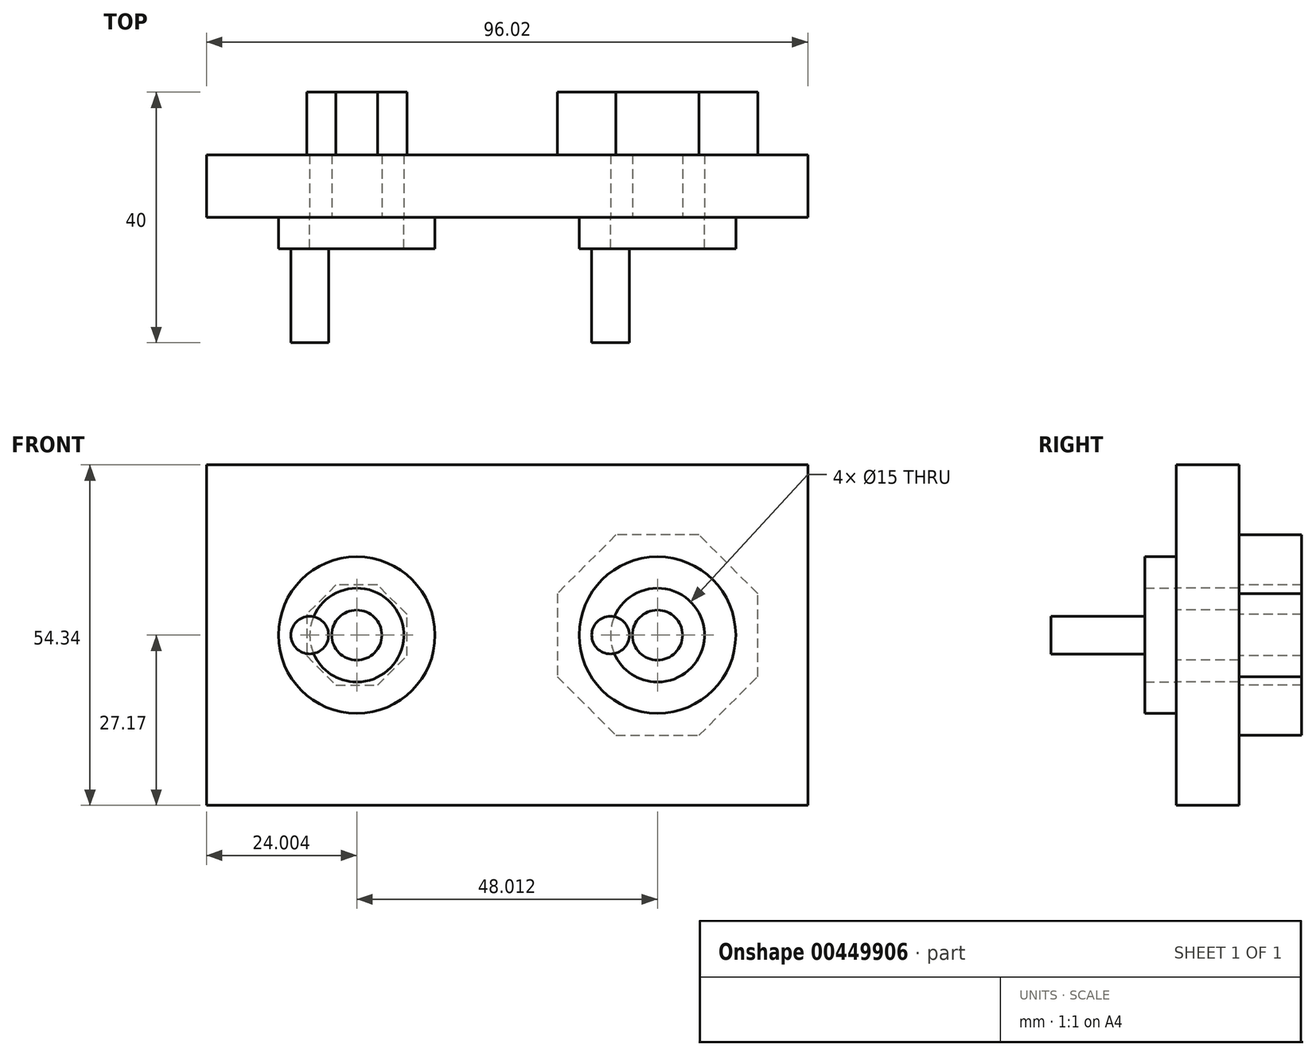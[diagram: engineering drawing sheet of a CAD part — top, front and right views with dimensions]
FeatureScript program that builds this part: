
annotation { "Feature Type Name" : "Feature", "Feature Type Description" : "" }
export const myFeature = defineFeature(function(context is Context, id is Id, definition is map)
    precondition{}
    {
        {
            var Q0;
            Q0=qCreatedBy(makeId("Front.planeOp"),FACE);
            var sketch = newSketch(context, id + "F0", { "sketchPlane" : qUnion([Q0])});
            skLineSegment(sketch, "E0.bottom", {"start": v(-48.01, 27.17) * mm, "end": v(48.01, 27.17) * mm});
            skLineSegment(sketch, "E0.top", {"start": v(-48.01, -27.17) * mm, "end": v(48.01, -27.17) * mm});
            skLineSegment(sketch, "E0.left", {"start": v(-48.01, 27.17) * mm, "end": v(-48.01, -27.17) * mm});
            skLineSegment(sketch, "E0.right", {"start": v(48.01, 27.17) * mm, "end": v(48.01, -27.17) * mm});
            skPoint(sketch, "E0.middle", {"position": v(0, 0) * mm});
            skSolve(sketch);
        }
        {
            var Q0;
            Q0=makeQuery(id+"F0.imprint","IMPRINT",FACE,{"disambiguationData":[TD([[makeQuery(id+"F0.imprint","IMPRINT",EDGE,{"derivedFrom":sQuery(id+"F0.wireOp",EDGE,"E0.bottom")}),-1.0]])]});
            extrude(context, id + "F1", {"entities" : qUnion([Q0]), "depth" : 10 * mm});
        }
        {
            var Q0;
            Q0=makeQuery(id+"F1.opExtrude","CAP_FACE",FACE,{"disambiguationData":[OSD([sQuery(id+"F0.wireOp",EDGE,"E0.bottom"),sQuery(id+"F0.wireOp",EDGE,"E0.top"),sQuery(id+"F0.wireOp",EDGE,"E0.left"),sQuery(id+"F0.wireOp",EDGE,"E0.right")])],"isStart":false});
            var sketch = newSketch(context, id + "F2", { "sketchPlane" : qUnion([Q0])});
            skLineSegment(sketch, "E1", {"start": v(0, 0) * mm, "end": v(-48.01, 0) * mm, "construction": true});
            skLineSegment(sketch, "E2", {"start": v(0, 0) * mm, "end": v(48.01, 0) * mm, "construction": true});
            skCircle(sketch, "E3", {"center": v(-24, 0) * mm, "radius": 7.5 * mm});
            skCircle(sketch, "E4", {"center": v(24, 0) * mm, "radius": 7.5 * mm});
            skSolve(sketch);
        }
        {
            var Q0;
            Q0=makeQuery(id+"F2.imprint","IMPRINT",FACE,{"disambiguationData":[TD([[makeQuery(id+"F2.imprint","IMPRINT",EDGE,{"derivedFrom":sQuery(id+"F2.wireOp",EDGE,"E3")}),1.0]])]});
            var Q1;
            Q1=makeQuery(id+"F2.imprint","IMPRINT",FACE,{"disambiguationData":[TD([[makeQuery(id+"F2.imprint","IMPRINT",EDGE,{"derivedFrom":sQuery(id+"F2.wireOp",EDGE,"E4")}),1.0]])]});
            var Q2;
            Q2=makeQuery(id+"F1.opExtrude","CAP_FACE",FACE,{"disambiguationData":[OSD([sQuery(id+"F0.wireOp",EDGE,"E0.bottom"),sQuery(id+"F0.wireOp",EDGE,"E0.top"),sQuery(id+"F0.wireOp",EDGE,"E0.left"),sQuery(id+"F0.wireOp",EDGE,"E0.right")])],"isStart":true});
            extrude(context, id + "F3", {"entities" : qUnion([Q0, Q1]), "operationType" : NewBodyOperationType.REMOVE, "endBound" : BoundingType.UP_TO_SURFACE, "oppositeDirection" : true, "endBoundEntityFace" : qUnion([Q2]), "depth" : 25 * mm});
        }
        {
            var Q0;
            Q0=makeQuery(id+"F1.opExtrude","CAP_FACE",FACE,{"disambiguationData":[OSD([sQuery(id+"F0.wireOp",EDGE,"E0.bottom"),sQuery(id+"F0.wireOp",EDGE,"E0.top"),sQuery(id+"F0.wireOp",EDGE,"E0.left"),sQuery(id+"F0.wireOp",EDGE,"E0.right")])],"isStart":false});
            var sketch = newSketch(context, id + "F4", { "sketchPlane" : qUnion([Q0])});
            skCircle(sketch, "E5", {"center": v(-24, 0) * mm, "radius": 12.5 * mm});
            skCircle(sketch, "E6", {"center": v(24, 0) * mm, "radius": 12.5 * mm});
            skSolve(sketch);
        }
        {
            var Q0;
            Q0=makeQuery(id+"F4.imprint","IMPRINT",FACE,{"disambiguationData":[TD([[makeQuery(id+"F4.imprint","IMPRINT",EDGE,{"derivedFrom":sQuery(id+"F4.wireOp",EDGE,"E5")}),1.0]])]});
            var Q1;
            Q1=makeQuery(id+"F4.imprint","IMPRINT",FACE,{"disambiguationData":[TD([[makeQuery(id+"F4.imprint","IMPRINT",EDGE,{"derivedFrom":sQuery(id+"F4.wireOp",EDGE,"E6")}),1.0]])]});
            var Q2;
            Q2=makeQuery(id+"F4.imprint","IMPRINT",FACE,{"disambiguationData":[TD([[makeQuery(id+"F4.imprint","IMPRINT",EDGE,{"derivedFrom":makeQuery(id+"F3.boolean.opBoolean","COPY",EDGE,{"derivedFrom":makeQuery(id+"F3.opExtrude","CAP_EDGE",EDGE,{"disambiguationData":[OSD([sQuery(id+"F2.wireOp",EDGE,"E4")])],"isStart":true})})}),1.0]])]});
            var Q3;
            Q3=makeQuery(id+"F4.imprint","IMPRINT",FACE,{"disambiguationData":[TD([[makeQuery(id+"F4.imprint","IMPRINT",EDGE,{"derivedFrom":makeQuery(id+"F3.boolean.opBoolean","COPY",EDGE,{"derivedFrom":makeQuery(id+"F3.opExtrude","CAP_EDGE",EDGE,{"disambiguationData":[OSD([sQuery(id+"F2.wireOp",EDGE,"E3")])],"isStart":true})})}),1.0]])]});
            extrude(context, id + "F5", {"entities" : qUnion([Q0, Q1, Q2, Q3]), "depth" : 5 * mm});
        }
        {
            var Q0;
            Q0=makeQuery(id+"F5.opExtrude","CAP_FACE",FACE,{"disambiguationData":[OSD([sQuery(id+"F4.wireOp",EDGE,"E5")])],"isStart":true});
            var sketch = newSketch(context, id + "F6", { "sketchPlane" : qUnion([Q0])});
            skCircle(sketch, "E7", {"center": v(24, 0) * mm, "radius": 4 * mm});
            skCircle(sketch, "E8.0", {"center": v(-24, 0) * mm, "radius": 7.5 * mm});
            skCircle(sketch, "E9", {"center": v(-24, 0) * mm, "radius": 4 * mm});
            skSolve(sketch);
        }
        {
            var Q0;
            Q0=makeQuery(id+"F6.imprint","IMPRINT",FACE,{"disambiguationData":[TD([[makeQuery(id+"F6.imprint","IMPRINT",EDGE,{"derivedFrom":sQuery(id+"F6.wireOp",EDGE,"E9")}),1.0]])]});
            var Q1;
            Q1=makeQuery(id+"F6.imprint","IMPRINT",FACE,{"disambiguationData":[TD([[makeQuery(id+"F6.imprint","IMPRINT",EDGE,{"derivedFrom":sQuery(id+"F6.wireOp",EDGE,"E7")}),1.0]])]});
            var Q2;
            Q2=makeQuery(id+"F1.opExtrude","CAP_FACE",FACE,{"disambiguationData":[OSD([sQuery(id+"F0.wireOp",EDGE,"E0.bottom"),sQuery(id+"F0.wireOp",EDGE,"E0.top"),sQuery(id+"F0.wireOp",EDGE,"E0.left"),sQuery(id+"F0.wireOp",EDGE,"E0.right")])],"isStart":true});
            extrude(context, id + "F7", {"entities" : qUnion([Q0, Q1]), "operationType" : NewBodyOperationType.ADD, "endBound" : BoundingType.UP_TO_SURFACE, "endBoundEntityFace" : qUnion([Q2]), "depth" : 25 * mm});
        }
        {
            var Q0;
            Q0=makeQuery(id+"F7.opExtrude","CAP_FACE",FACE,{"disambiguationData":[OSD([sQuery(id+"F6.wireOp",EDGE,"E9")])],"isStart":false});
            var sketch = newSketch(context, id + "F8", { "sketchPlane" : qUnion([Q0])});
            skCircle(sketch, "E10.cCircle", {"center": v(-24, 0) * mm, "radius": 16 * mm, "construction": true});
            skLineSegment(sketch, "E10.0", {"start": v(-8, 6.63) * mm, "end": v(-8, -6.63) * mm});
            skLineSegment(sketch, "E10.1", {"start": v(-8, -6.63) * mm, "end": v(-17.38, -16) * mm});
            skLineSegment(sketch, "E10.2", {"start": v(-17.38, -16) * mm, "end": v(-30.63, -16) * mm});
            skLineSegment(sketch, "E10.3", {"start": v(-30.63, -16) * mm, "end": v(-40, -6.63) * mm});
            skLineSegment(sketch, "E10.4", {"start": v(-40, -6.63) * mm, "end": v(-40, 6.63) * mm});
            skLineSegment(sketch, "E10.5", {"start": v(-40, 6.63) * mm, "end": v(-30.63, 16) * mm});
            skLineSegment(sketch, "E10.6", {"start": v(-30.63, 16) * mm, "end": v(-17.38, 16) * mm});
            skLineSegment(sketch, "E10.7", {"start": v(-17.38, 16) * mm, "end": v(-8, 6.63) * mm});
            skPoint(sketch, "E10.0.midPoint", {"position": v(-8, 0) * mm});
            skCircle(sketch, "E11.0.0", {"center": v(24, 0) * mm, "radius": 4 * mm, "construction": true});
            skCircle(sketch, "E12.cCircle", {"center": v(24, 0) * mm, "radius": 8 * mm, "construction": true});
            skLineSegment(sketch, "E12.0", {"start": v(20.7, 8) * mm, "end": v(27.32, 8) * mm});
            skLineSegment(sketch, "E12.1", {"start": v(27.32, 8) * mm, "end": v(32, 3.31) * mm});
            skLineSegment(sketch, "E12.2", {"start": v(32, 3.31) * mm, "end": v(32, -3.31) * mm});
            skLineSegment(sketch, "E12.3", {"start": v(32, -3.31) * mm, "end": v(27.32, -8) * mm});
            skLineSegment(sketch, "E12.4", {"start": v(27.32, -8) * mm, "end": v(20.7, -8) * mm});
            skLineSegment(sketch, "E12.5", {"start": v(20.7, -8) * mm, "end": v(16, -3.31) * mm});
            skLineSegment(sketch, "E12.6", {"start": v(16, -3.31) * mm, "end": v(16, 3.31) * mm});
            skLineSegment(sketch, "E12.7", {"start": v(16, 3.31) * mm, "end": v(20.7, 8) * mm});
            skPoint(sketch, "E12.0.midPoint", {"position": v(24, 8) * mm});
            skSolve(sketch);
        }
        {
            var Q0;
            Q0=makeQuery(id+"F8.imprint","IMPRINT",FACE,{"disambiguationData":[TD([[makeQuery(id+"F8.imprint","IMPRINT",EDGE,{"derivedFrom":makeQuery(id+"F7.opExtrude","CAP_EDGE",EDGE,{"disambiguationData":[OSD([sQuery(id+"F6.wireOp",EDGE,"E9")])],"isStart":false})}),-1.0]])]});
            var Q1;
            Q1=makeQuery(id+"F8.imprint","IMPRINT",FACE,{"disambiguationData":[TD([[makeQuery(id+"F8.imprint","IMPRINT",EDGE,{"derivedFrom":sQuery(id+"F8.wireOp",EDGE,"E12.0")}),-1.0]])]});
            var Q2;
            Q2=makeQuery(id+"F8.imprint","IMPRINT",FACE,{"disambiguationData":[TD([[makeQuery(id+"F8.imprint","IMPRINT",EDGE,{"derivedFrom":sQuery(id+"F8.wireOp",EDGE,"E10.0")}),-1.0]])]});
            extrude(context, id + "F9", {"entities" : qUnion([Q0, Q1, Q2]), "depth" : 10 * mm});
        }
        {
            var Q0;
            Q0=makeQuery(id+"F5.opExtrude","CAP_FACE",FACE,{"disambiguationData":[OSD([sQuery(id+"F4.wireOp",EDGE,"E6")])],"isStart":false});
            var sketch = newSketch(context, id + "F10", { "sketchPlane" : qUnion([Q0])});
            skCircle(sketch, "E13", {"center": v(16.5, 0) * mm, "radius": 3 * mm});
            skCircle(sketch, "E14", {"center": v(-31.5, 0) * mm, "radius": 3 * mm});
            skSolve(sketch);
        }
        {
            var Q0;
            Q0=makeQuery(id+"F10.imprint","IMPRINT",FACE,{"disambiguationData":[TD([[makeQuery(id+"F10.imprint","IMPRINT",EDGE,{"derivedFrom":sQuery(id+"F10.wireOp",EDGE,"E13")}),1.0]])]});
            var Q1;
            Q1=makeQuery(id+"F10.imprint","IMPRINT",FACE,{"disambiguationData":[TD([[makeQuery(id+"F10.imprint","IMPRINT",EDGE,{"derivedFrom":sQuery(id+"F10.wireOp",EDGE,"E14")}),1.0]])]});
            extrude(context, id + "F11", {"entities" : qUnion([Q0, Q1]), "depth" : 15 * mm});
        }
    });
